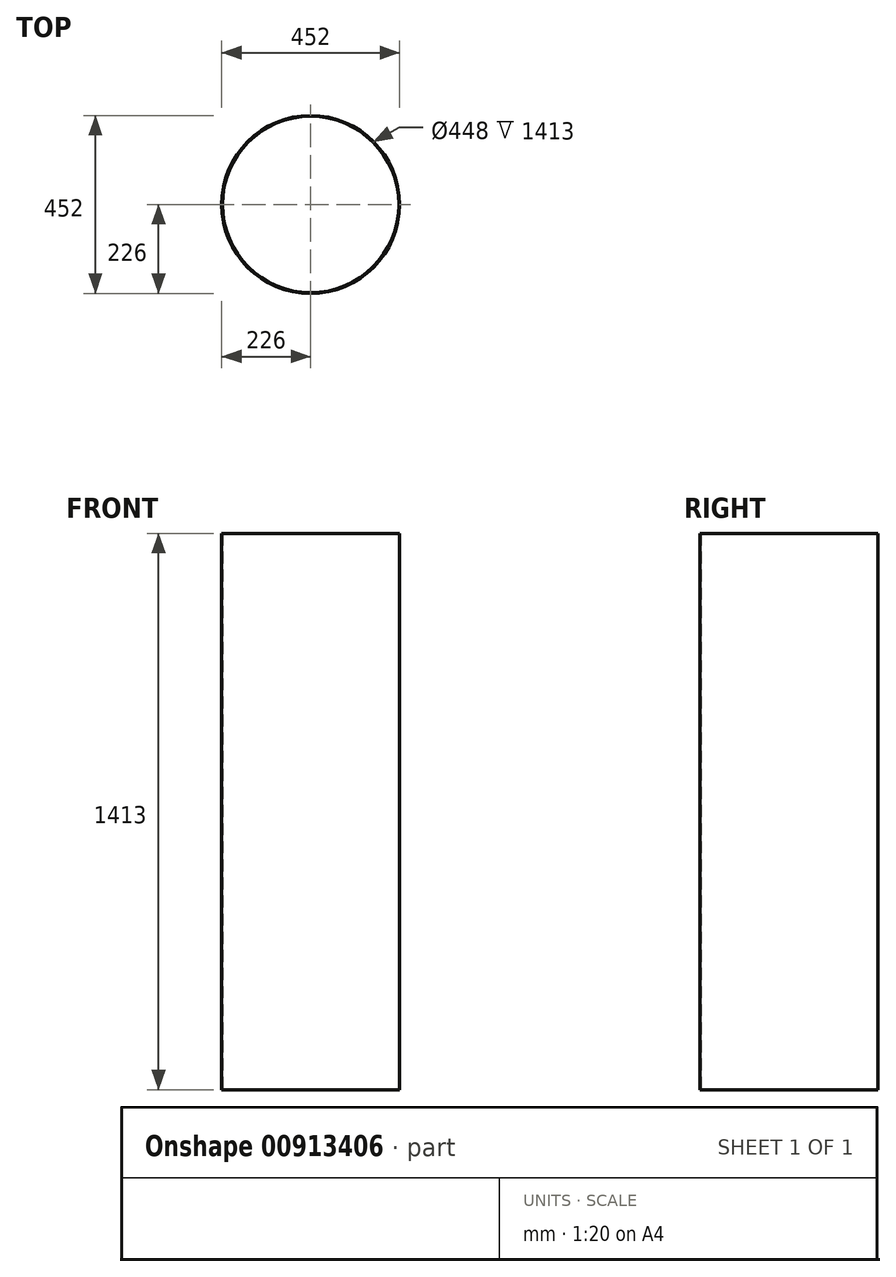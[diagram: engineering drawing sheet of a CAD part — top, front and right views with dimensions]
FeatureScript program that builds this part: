
annotation { "Feature Type Name" : "Feature", "Feature Type Description" : "" }
export const myFeature = defineFeature(function(context is Context, id is Id, definition is map)
    precondition{}
    {
        {
            var Q0;
            Q0=qCreatedBy(makeId("Front.planeOp"),FACE);
            var sketch = newSketch(context, id + "F0", { "sketchPlane" : qUnion([Q0])});
            skLineSegment(sketch, "E0", {"start": v(0, -104.19) * mm, "end": v(0, 110.8) * mm, "construction": true});
            skLineSegment(sketch, "E1", {"start": v(-88.73, 0) * mm, "end": v(119.36, 0) * mm, "construction": true});
            skLineSegment(sketch, "E2.0", {"start": v(224, 706.5) * mm, "end": v(226, 706.5) * mm});
            skLineSegment(sketch, "E3.0", {"start": v(224, -706.5) * mm, "end": v(226, -706.5) * mm});
            skLineSegment(sketch, "E4.0", {"start": v(226, -706.5) * mm, "end": v(226, 706.5) * mm});
            skLineSegment(sketch, "E5.0", {"start": v(224, -706.5) * mm, "end": v(224, 706.5) * mm});
            skSolve(sketch);
        }
        {
            var Q0;
            Q0=makeQuery(id+"F0.imprint","IMPRINT",FACE,{"disambiguationData":[TD([[makeQuery(id+"F0.imprint","IMPRINT",EDGE,{"derivedFrom":sQuery(id+"F0.wireOp",EDGE,"E2.0")}),-1.0]])]});
            var Q1;
            Q1=sQuery(id+"F0.wireOp",EDGE,"E0");
            revolve(context, id + "F1", {"surfaceOperationType" : NewSurfaceOperationType.NEW, "entities" : qUnion([Q0]), "axis" : qUnion([Q1]), "revolveType" : RevolveType.FULL});
        }
    });
